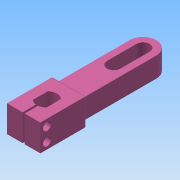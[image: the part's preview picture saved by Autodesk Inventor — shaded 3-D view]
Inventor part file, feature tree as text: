
AUTODESK INVENTOR PART (.ipt)
format: ipt  version: 2015 (Build 190159000, 159)  size: 178,176 bytes
history: native  units: mm
features: extrude x6, sketch x6, thread x2, fillet x2
ambient origin geometry x8: Origin, YZ Plane, XZ Plane, XY Plane, X Axis, Y Axis, Z Axis, Center Point
bodies: 实体1 (feature_tree)
feature tree (16):
  extrude  "拉伸1"  Depth=35.0mm
  extrude  "拉伸2"  Depth=20.0mm
  extrude  "拉伸3"  Depth=15.0mm
  extrude  "拉伸4"  Depth=10.0mm
  extrude  "拉伸5"  Depth=10.0mm
  thread  "螺纹1"  [1 undecoded]
  thread  "螺纹2"  [1 undecoded]
  extrude  "拉伸6"  Depth=20.0mm TaperAngle=0.0deg
  fillet  "圆角1"  Radius=15.0mm
  fillet  "圆角2"  Radius=2.5mm
  sketch  "草图1"  dims[d0=25.0mm d1=35.0mm]
  sketch  "草图2"  dims[d2=15.0mm d3=20.0mm]
  sketch  "草图3"  dims[d5=20.0mm d6=0.0mm d7=15.0mm]
  sketch  "草图4"  dims[d8=1.5mm d9=10.0mm]
  sketch  "草图5"  dims[d10=10.0mm d11=10.0mm d12=50.0mm d13=82.0mm]
  sketch  "草图6"  dims[d14=10.0mm d15=20.0mm d16=0.0mm d17=15.0mm d18=2.5mm d19=20.0mm d20=0.0mm d21=3.0mm d22=3.0mm d23=5.0mm d24=5.0mm d25=5.0mm d26=5.0mm d27=20.0mm d28=0.0mm d29=6.0mm d30=6.0mm d31=4.0mm d32=0.0mm d33=10.0mm d34=0.0mm d35=10.0mm d36=0.0mm d37=10.0mm d38=5.59017mm d39=20.0mm d40=0.0mm d41=10.0mm d42=2.0mm]
note: 2 required parameter values undecoded (feature->parameter linkage not recoverable at this tier; creation-order binding heuristic only, values carry confidence <= 0.55)
